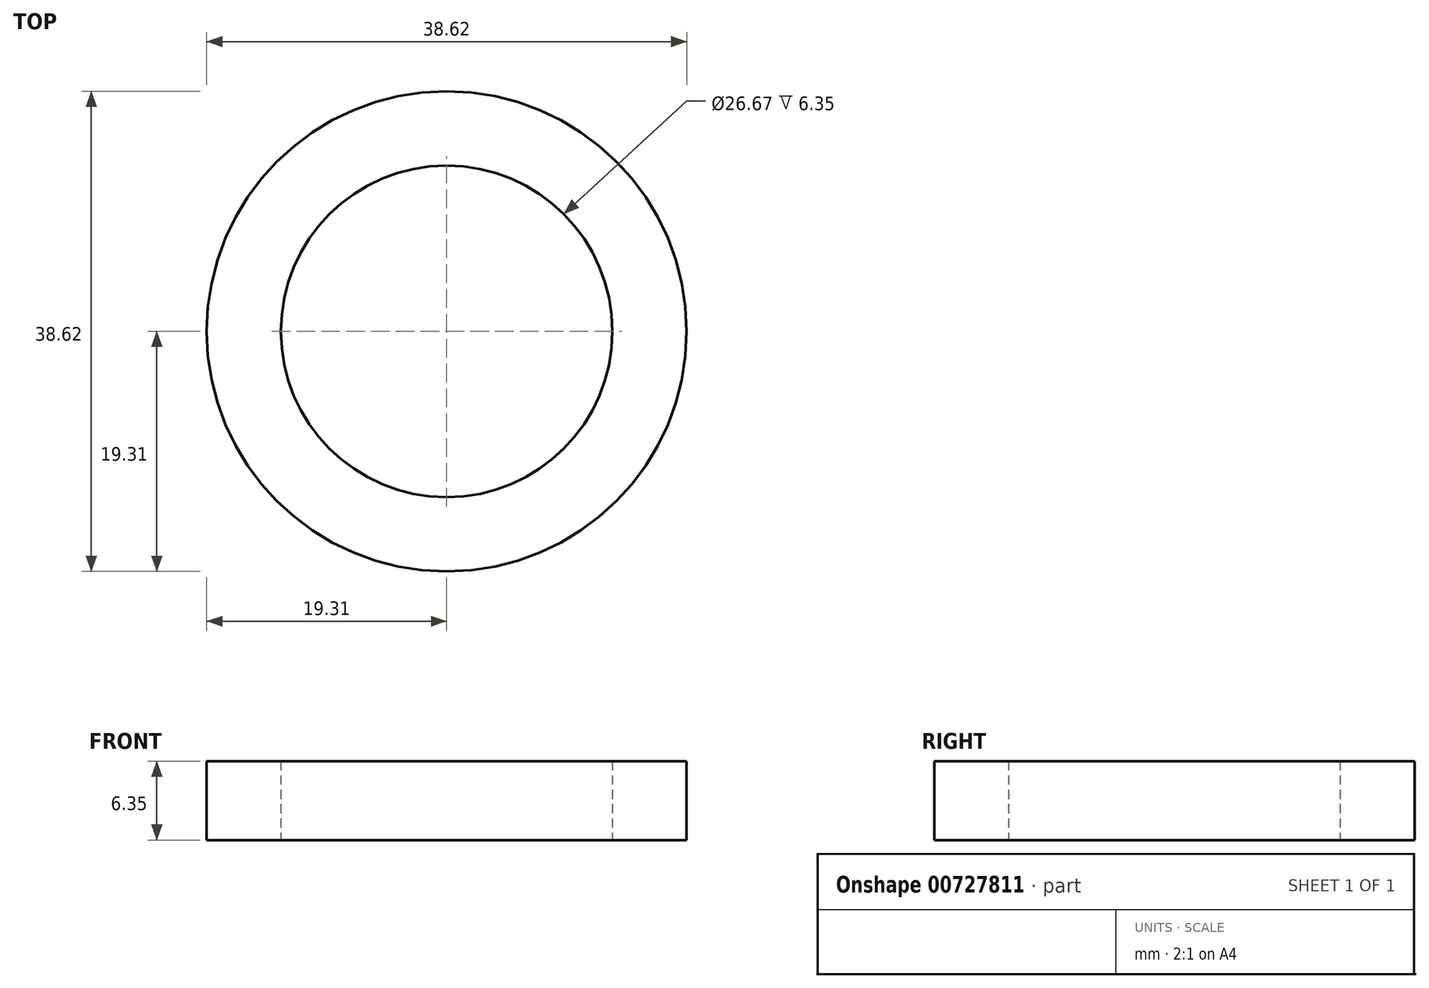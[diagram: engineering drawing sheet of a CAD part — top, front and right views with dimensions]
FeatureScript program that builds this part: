
annotation { "Feature Type Name" : "Feature", "Feature Type Description" : "" }
export const myFeature = defineFeature(function(context is Context, id is Id, definition is map)
    precondition{}
    {
        {
            var Q0;
            Q0=qCreatedBy(makeId("Top.planeOp"),FACE);
            var sketch = newSketch(context, id + "F0", { "sketchPlane" : qUnion([Q0])});
            skCircle(sketch, "E0", {"center": v(0, 0) * mm, "radius": 13.33 * mm});
            skCircle(sketch, "E1", {"center": v(0, 0) * mm, "radius": 19.3 * mm});
            skSolve(sketch);
        }
        {
            var Q0;
            Q0=makeQuery(id+"F0.imprint","IMPRINT",FACE,{"disambiguationData":[TD([[makeQuery(id+"F0.imprint","IMPRINT",EDGE,{"derivedFrom":sQuery(id+"F0.wireOp",EDGE,"E0")}),-1.0]])]});
            extrude(context, id + "F1", {"entities" : qUnion([Q0]), "depth" : 6.35 * mm, "offsetDistance" : 25.4 * mm});
        }
    });
